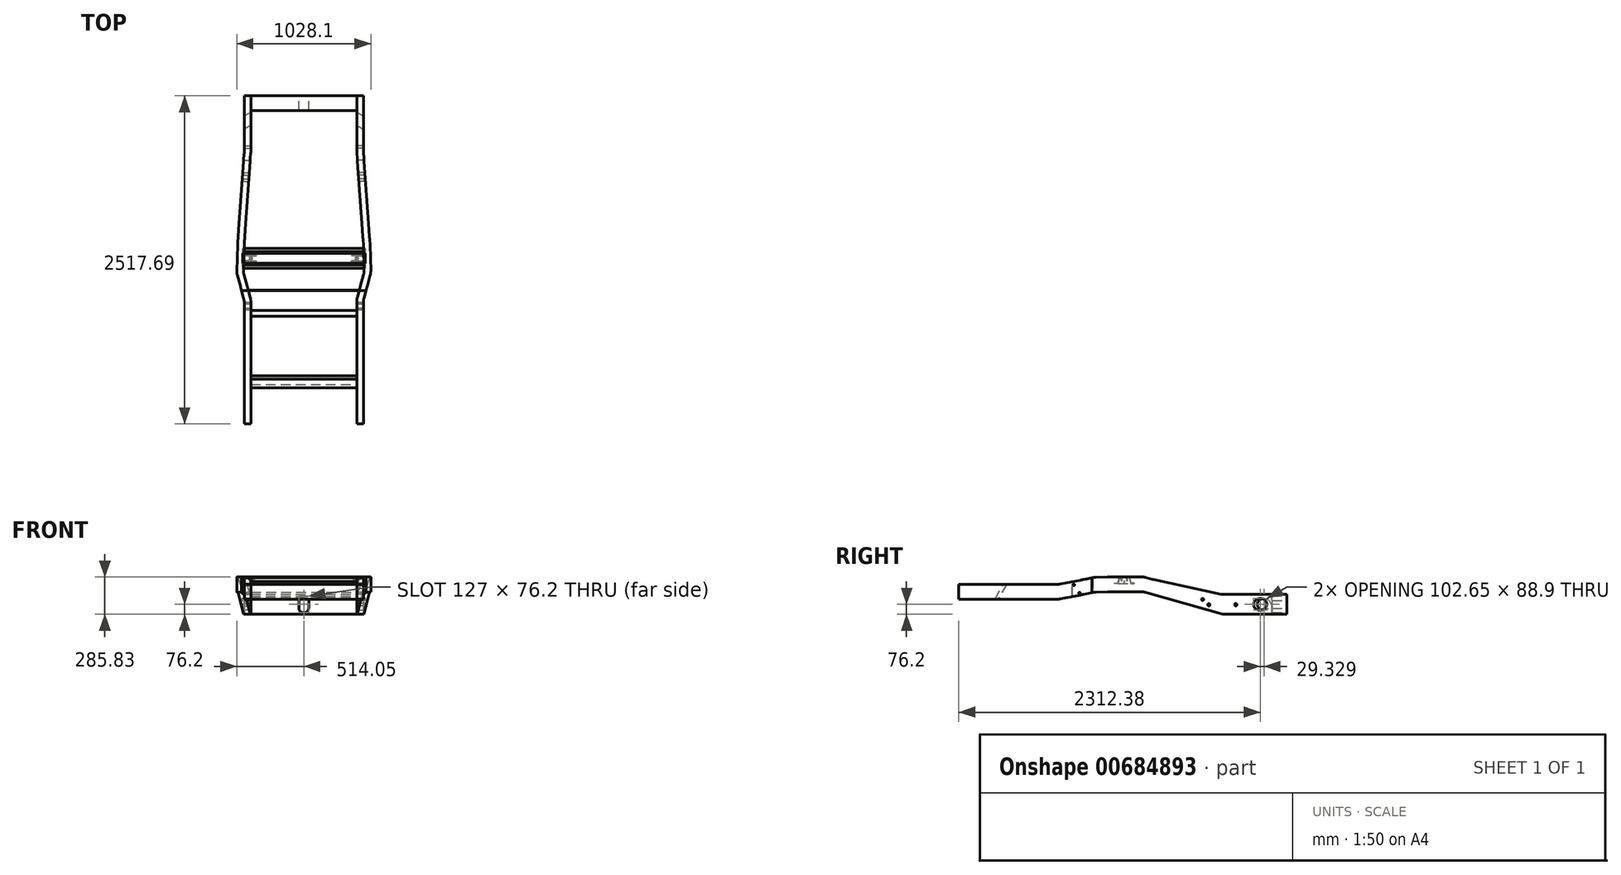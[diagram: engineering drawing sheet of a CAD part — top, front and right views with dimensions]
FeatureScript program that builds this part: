
annotation { "Feature Type Name" : "Feature", "Feature Type Description" : "" }
export const myFeature = defineFeature(function(context is Context, id is Id, definition is map)
    precondition{}
    {
        {
            var Q0;
            Q0=qCreatedBy(makeId("Top.planeOp"),FACE);
            var sketch = newSketch(context, id + "F0", { "sketchPlane" : qUnion([Q0])});
            skLineSegment(sketch, "E0", {"start": v(0, 1936.1) * mm, "end": v(0, -5906.31) * mm, "construction": true});
            skLineSegment(sketch, "E1", {"start": v(431.8, 0) * mm, "end": v(431.8, -431.8) * mm});
            skLineSegment(sketch, "E2", {"start": v(431.8, -431.8) * mm, "end": v(482.6, -1141.18) * mm});
            skLineSegment(sketch, "E3", {"start": v(482.6, -1141.18) * mm, "end": v(488.95, -1356.99) * mm});
            skLineSegment(sketch, "E4", {"start": v(488.95, -1356.99) * mm, "end": v(431.8, -1565.19) * mm});
            skLineSegment(sketch, "E5", {"start": v(431.8, -1565.19) * mm, "end": v(431.8, -2517.69) * mm});
            skLineSegment(sketch, "E6", {"start": v(431.8, -431.8) * mm, "end": v(431.8, -1285.92) * mm, "construction": true});
            skSolve(sketch);
        }
        {
            var Q0;
            Q0=qCreatedBy(makeId("Front.planeOp"),FACE);
            var Q1;
            Q1=sQuery(id+"F0.wireOp",VERTEX,"E1.start");
            cPlane(context, id + "F1", {"entities" : qUnion([Q0, Q1]), "cplaneType" : CPlaneType.PLANE_POINT, "offset" : 25.4 * mm, "width" : 152.4 * mm, "height" : 152.4 * mm});
        }
        {
            var Q0;
            Q0=qCreatedBy(id+"F1.planeOp",FACE);
            var sketch = newSketch(context, id + "F2", { "sketchPlane" : qUnion([Q0])});
            skLineSegment(sketch, "E7.bottom", {"start": v(406.4, 203.2) * mm, "end": v(457.2, 203.2) * mm});
            skLineSegment(sketch, "E7.top", {"start": v(406.4, -203.2) * mm, "end": v(457.2, -203.2) * mm});
            skLineSegment(sketch, "E7.left", {"start": v(406.4, 203.2) * mm, "end": v(406.4, -203.2) * mm});
            skLineSegment(sketch, "E7.right", {"start": v(457.2, 203.2) * mm, "end": v(457.2, -203.2) * mm});
            skPoint(sketch, "E7.middle", {"position": v(431.8, 0) * mm});
            skLineSegment(sketch, "E8", {"start": v(0, 0) * mm, "end": v(572.75, 0) * mm, "construction": true});
            skSolve(sketch);
        }
        {
            var Q0;
            Q0 = qSketchRegion(id + "F2", true);
            var Q1;
            Q1 = qConstructionFilter(qBodyType(qCreatedBy(id + "F0" ,EDGE), BodyType.WIRE), ConstructionObject.NO);
            sweep(context, id + "F3", {"profiles" : qUnion([Q0]), "path" : qUnion([Q1])});
        }
        {
            var Q0;
            Q0=qCreatedBy(makeId("Right.planeOp"),FACE);
            var sketch = newSketch(context, id + "F4", { "sketchPlane" : qUnion([Q0])});
            skLineSegment(sketch, "E9", {"start": v(0, -203.2) * mm, "end": v(-493.71, -203.2) * mm});
            skLineSegment(sketch, "E10", {"start": v(-493.71, -203.2) * mm, "end": v(-1091.9, -31.67) * mm});
            skLineSegment(sketch, "E11", {"start": v(-1091.9, -31.67) * mm, "end": v(-1371.3, -31.67) * mm});
            skLineSegment(sketch, "E12", {"start": v(-1371.3, -31.67) * mm, "end": v(-1472.9, -33.44) * mm});
            skLineSegment(sketch, "E13", {"start": v(-1371.3, -31.67) * mm, "end": v(-1529.34, -31.67) * mm, "construction": true});
            skLineSegment(sketch, "E14", {"start": v(-1472.9, -33.44) * mm, "end": v(-1747.16, -86.76) * mm});
            skLineSegment(sketch, "E15", {"start": v(-1747.16, -86.76) * mm, "end": v(-2517.69, -86.76) * mm});
            skLineSegment(sketch, "E16", {"start": v(-2517.69, -86.76) * mm, "end": v(-2517.69, -253.61) * mm});
            skLineSegment(sketch, "E17", {"start": v(-2517.69, -253.61) * mm, "end": v(0, -269.23) * mm});
            skLineSegment(sketch, "E18", {"start": v(0, -269.23) * mm, "end": v(0, -203.2) * mm});
            skLineSegment(sketch, "E19", {"start": v(0, -50.8) * mm, "end": v(-493.71, -50.8) * mm});
            skLineSegment(sketch, "E20", {"start": v(-493.71, -50.8) * mm, "end": v(-1028.7, 64.5) * mm});
            skLineSegment(sketch, "E21", {"start": v(-1028.7, 64.5) * mm, "end": v(-1028.7, -49.8) * mm, "construction": true});
            skLineSegment(sketch, "E22", {"start": v(-1091.9, -31.67) * mm, "end": v(-1091.9, 82.63) * mm, "construction": true});
            skLineSegment(sketch, "E23", {"start": v(-1371.3, -31.67) * mm, "end": v(-1371.3, 82.63) * mm, "construction": true});
            skLineSegment(sketch, "E24", {"start": v(-1472.9, -33.44) * mm, "end": v(-1472.9, 80.86) * mm, "construction": true});
            skLineSegment(sketch, "E25", {"start": v(-1747.16, -86.76) * mm, "end": v(-1747.16, 27.54) * mm, "construction": true});
            skLineSegment(sketch, "E26", {"start": v(-1028.7, 64.5) * mm, "end": v(-1091.9, 82.63) * mm});
            skLineSegment(sketch, "E27", {"start": v(-1091.9, 82.63) * mm, "end": v(-1371.3, 82.63) * mm});
            skLineSegment(sketch, "E28", {"start": v(-1472.9, 80.86) * mm, "end": v(-1747.16, 27.54) * mm});
            skLineSegment(sketch, "E29", {"start": v(-1472.9, 80.86) * mm, "end": v(-1371.3, 82.63) * mm});
            skLineSegment(sketch, "E30", {"start": v(-2517.69, -86.76) * mm, "end": v(-2517.69, 27.54) * mm, "construction": true});
            skLineSegment(sketch, "E31", {"start": v(-1747.16, 27.54) * mm, "end": v(-2517.69, 27.54) * mm});
            skLineSegment(sketch, "E32", {"start": v(-2517.69, 27.54) * mm, "end": v(-2517.69, 524.74) * mm});
            skLineSegment(sketch, "E33", {"start": v(-2517.69, 524.74) * mm, "end": v(0, 524.74) * mm});
            skLineSegment(sketch, "E34", {"start": v(0, 524.74) * mm, "end": v(0, -50.8) * mm});
            skSolve(sketch);
        }
        {
            var Q0;
            Q0 = qSketchRegion(id + "F4", true);
            var Q1;
            Q1=makeQuery(id+"F3.opSweep","SWEPT_FACE",FACE,{"disambiguationData":[OSD([sQuery(id+"F0.wireOp",EDGE,"1umSsKEu-dJId-BIwL-yde3-wRK5SwyTBX2N"),sQuery(id+"F2.wireOp",EDGE,"E7.right")])]});
            extrude(context, id + "F5", {"entities" : qUnion([Q0]), "operationType" : NewBodyOperationType.REMOVE, "depth" : 609.6 * mm, "endBoundEntityFace" : qUnion([Q1]), "offsetDistance" : 25.4 * mm});
        }
        {
            var Q0;
            Q0=makeQuery(id+"F3.opSweep","SWEPT_FACE",FACE,{"disambiguationData":[OSD([sQuery(id+"F0.wireOp",EDGE,"E1"),sQuery(id+"F2.wireOp",EDGE,"E7.left")])]});
            var sketch = newSketch(context, id + "F6", { "sketchPlane" : qUnion([Q0])});
            skLineSegment(sketch, "E35", {"start": v(-416.37, -129.41) * mm, "end": v(600.08, -129.41) * mm, "construction": true});
            skLineSegment(sketch, "E36", {"start": v(393.7, 39.46) * mm, "end": v(393.7, -270.74) * mm, "construction": true});
            skLineSegment(sketch, "E37", {"start": v(393.7, -88.9) * mm, "end": v(863.06, -88.9) * mm, "construction": true});
            skLineSegment(sketch, "E38", {"start": v(600.08, 71) * mm, "end": v(600.08, -269.25) * mm, "construction": true});
            skLineSegment(sketch, "E39", {"start": v(647.7, 77.42) * mm, "end": v(647.7, -282.1) * mm, "construction": true});
            skCircle(sketch, "E40", {"center": v(600.08, -129.41) * mm, "radius": 8.9 * mm});
            skCircle(sketch, "E41", {"center": v(647.7, -88.9) * mm, "radius": 8.9 * mm});
            skCircle(sketch, "E42", {"center": v(393.7, -129.41) * mm, "radius": 8.9 * mm});
            skSolve(sketch);
        }
        {
            var Q0;
            Q0 = qSketchRegion(id + "F6", true);
            extrude(context, id + "F7", {"entities" : qUnion([Q0]), "operationType" : NewBodyOperationType.REMOVE, "oppositeDirection" : true, "depth" : 508 * mm, "offsetDistance" : 25.4 * mm, "symmetric" : true});
        }
        {
            var Q0;
            Q0=makeQuery(id+"F5.boolean.opBoolean","COPY",EDGE,{"derivedFrom":makeQuery(id+"F5.opExtrude","SWEPT_EDGE",EDGE,{"disambiguationData":[OSD([sQuery(id+"F4.wireOp",EDGE,"E19"),sQuery(id+"F4.wireOp",EDGE,"E20")])]})});
            var Q1;
            Q1=makeQuery(id+"F3.opSweep","MID_CAP_EDGE",EDGE,{"disambiguationData":[OSD([sQuery(id+"F0.wireOp",VERTEX,"E2.start"),sQuery(id+"F2.wireOp",EDGE,"E7.left")])],"capPos":1.0});
            var Q2;
            Q2=makeQuery(id+"F5.boolean.opBoolean","COPY",EDGE,{"derivedFrom":makeQuery(id+"F5.opExtrude","SWEPT_EDGE",EDGE,{"disambiguationData":[OSD([sQuery(id+"F4.wireOp",EDGE,"E20"),sQuery(id+"F4.wireOp",EDGE,"E26")])]})});
            var Q3;
            Q3=makeQuery(id+"F5.boolean.opBoolean","COPY",EDGE,{"derivedFrom":makeQuery(id+"F5.opExtrude","SWEPT_EDGE",EDGE,{"disambiguationData":[OSD([sQuery(id+"F4.wireOp",EDGE,"E26"),sQuery(id+"F4.wireOp",EDGE,"E27")])]})});
            var Q4;
            Q4=makeQuery(id+"F3.opSweep","MID_CAP_EDGE",EDGE,{"disambiguationData":[OSD([sQuery(id+"F0.wireOp",VERTEX,"E3.start"),sQuery(id+"F2.wireOp",EDGE,"E7.left")])],"capPos":2.0});
            var Q5;
            Q5=makeQuery(id+"F5.boolean.opBoolean","COPY",EDGE,{"derivedFrom":makeQuery(id+"F5.opExtrude","SWEPT_EDGE",EDGE,{"disambiguationData":[OSD([sQuery(id+"F4.wireOp",EDGE,"E27"),sQuery(id+"F4.wireOp",EDGE,"E29")])]})});
            var Q6;
            Q6=makeQuery(id+"F5.boolean.opBoolean","COPY",EDGE,{"derivedFrom":makeQuery(id+"F5.opExtrude","SWEPT_EDGE",EDGE,{"disambiguationData":[OSD([sQuery(id+"F4.wireOp",EDGE,"E28"),sQuery(id+"F4.wireOp",EDGE,"E29")])]})});
            var Q7;
            Q7=makeQuery(id+"F3.opSweep","MID_CAP_EDGE",EDGE,{"disambiguationData":[OSD([sQuery(id+"F0.wireOp",VERTEX,"E4.start"),sQuery(id+"F2.wireOp",EDGE,"E7.left")])],"capPos":3.0});
            var Q8;
            Q8=makeQuery(id+"F3.opSweep","MID_CAP_EDGE",EDGE,{"disambiguationData":[OSD([sQuery(id+"F0.wireOp",VERTEX,"E5.start"),sQuery(id+"F2.wireOp",EDGE,"E7.left")])],"capPos":4.0});
            var Q9;
            Q9=makeQuery(id+"F5.boolean.opBoolean","COPY",EDGE,{"derivedFrom":makeQuery(id+"F5.opExtrude","SWEPT_EDGE",EDGE,{"disambiguationData":[OSD([sQuery(id+"F4.wireOp",EDGE,"E28"),sQuery(id+"F4.wireOp",EDGE,"E31")])]})});
            var Q10;
            Q10=makeQuery(id+"F5.boolean.opBoolean","COPY",EDGE,{"derivedFrom":makeQuery(id+"F5.opExtrude","SWEPT_EDGE",EDGE,{"disambiguationData":[OSD([sQuery(id+"F4.wireOp",EDGE,"E14"),sQuery(id+"F4.wireOp",EDGE,"E15")])]})});
            var Q11;
            Q11=makeQuery(id+"F5.boolean.opBoolean","COPY",EDGE,{"derivedFrom":makeQuery(id+"F5.opExtrude","SWEPT_EDGE",EDGE,{"disambiguationData":[OSD([sQuery(id+"F4.wireOp",EDGE,"E12"),sQuery(id+"F4.wireOp",EDGE,"E14")])]})});
            var Q12;
            Q12=makeQuery(id+"F5.boolean.opBoolean","COPY",EDGE,{"derivedFrom":makeQuery(id+"F5.opExtrude","SWEPT_EDGE",EDGE,{"disambiguationData":[OSD([sQuery(id+"F4.wireOp",EDGE,"E11"),sQuery(id+"F4.wireOp",EDGE,"E12")])]})});
            var Q13;
            Q13=makeQuery(id+"F5.boolean.opBoolean","COPY",EDGE,{"derivedFrom":makeQuery(id+"F5.opExtrude","SWEPT_EDGE",EDGE,{"disambiguationData":[OSD([sQuery(id+"F4.wireOp",EDGE,"E10"),sQuery(id+"F4.wireOp",EDGE,"E11")])]})});
            var Q14;
            Q14=makeQuery(id+"F5.boolean.opBoolean","COPY",EDGE,{"derivedFrom":makeQuery(id+"F5.opExtrude","SWEPT_EDGE",EDGE,{"disambiguationData":[OSD([sQuery(id+"F4.wireOp",EDGE,"E9"),sQuery(id+"F4.wireOp",EDGE,"E10")])]})});
            var Q15;
            Q15=makeQuery(id+"F3.opSweep","MID_CAP_EDGE",EDGE,{"disambiguationData":[OSD([sQuery(id+"F0.wireOp",VERTEX,"E2.start"),sQuery(id+"F2.wireOp",EDGE,"E7.right")])],"capPos":1.0});
            var Q16;
            Q16=makeQuery(id+"F3.opSweep","MID_CAP_EDGE",EDGE,{"disambiguationData":[OSD([sQuery(id+"F0.wireOp",VERTEX,"E3.start"),sQuery(id+"F2.wireOp",EDGE,"E7.right")])],"capPos":2.0});
            var Q17;
            Q17=makeQuery(id+"F3.opSweep","MID_CAP_EDGE",EDGE,{"disambiguationData":[OSD([sQuery(id+"F0.wireOp",VERTEX,"E4.start"),sQuery(id+"F2.wireOp",EDGE,"E7.right")])],"capPos":3.0});
            var Q18;
            Q18=makeQuery(id+"F3.opSweep","MID_CAP_EDGE",EDGE,{"disambiguationData":[OSD([sQuery(id+"F0.wireOp",VERTEX,"E5.start"),sQuery(id+"F2.wireOp",EDGE,"E7.right")])],"capPos":4.0});
            fillet(context, id + "F8", {"entities" : qUnion([Q0, Q1, Q2, Q3, Q4, Q5, Q6, Q7, Q8, Q9, Q10, Q11, Q12, Q13, Q14, Q15, Q16, Q17, Q18]), "radius" : 101.6 * mm, "tangentPropagation" : true, "allowEdgeOverflow" : false});
        }
        {
            var Q0;
            Q0=makeQuery(id+"F3.opSweep","SWEPT_BODY",BODY,{"disambiguationData":[OSD([sQuery(id+"F0.wireOp",EDGE,"zRG0IsD7-SMmf-8p0A-3XBu-xbHUB45AKsED"),sQuery(id+"F2.wireOp",EDGE,"E7.bottom"),sQuery(id+"F2.wireOp",EDGE,"E7.top"),sQuery(id+"F2.wireOp",EDGE,"E7.left"),sQuery(id+"F2.wireOp",EDGE,"E7.right")])]});
            var Q1;
            Q1=qCreatedBy(makeId("Right.planeOp"),FACE);
            mirror(context, id + "F9", {"entities" : qUnion([Q0]), "mirrorPlane" : qUnion([Q1])});
        }
        {
            var Q0;
            Q0=qCreatedBy(makeId("Right.planeOp"),FACE);
            var sketch = newSketch(context, id + "F10", { "sketchPlane" : qUnion([Q0])});
            skLineSegment(sketch, "E43", {"start": v(-2517.69, -86.76) * mm, "end": v(-1635.04, -86.76) * mm, "construction": true});
            skLineSegment(sketch, "E44", {"start": v(-1635.04, -86.76) * mm, "end": v(-1635.04, 22.37) * mm, "construction": true});
            skCircle(sketch, "E45", {"center": v(-1635.04, 22.37) * mm, "radius": 6.67 * mm});
            skCircle(sketch, "E46", {"center": v(-1590.59, -41.13) * mm, "radius": 6.67 * mm});
            skSolve(sketch);
        }
        {
            var Q0;
            Q0 = qSketchRegion(id + "F10", true);
            extrude(context, id + "F11", {"entities" : qUnion([Q0]), "operationType" : NewBodyOperationType.REMOVE, "oppositeDirection" : true, "depth" : 1016 * mm, "offsetDistance" : 25.4 * mm, "symmetric" : true});
        }
        {
            var Q0;
            Q0=makeQuery(id+"F3.opSweep","SWEPT_FACE",FACE,{"disambiguationData":[OSD([sQuery(id+"F0.wireOp",EDGE,"E1"),sQuery(id+"F2.wireOp",EDGE,"E7.left")])]});
            var sketch = newSketch(context, id + "F12", { "sketchPlane" : qUnion([Q0])});
            skLineSegment(sketch, "E47.bottom", {"start": v(0, -50.8) * mm, "end": v(114.3, -50.8) * mm});
            skLineSegment(sketch, "E47.top", {"start": v(0, -203.2) * mm, "end": v(114.3, -203.2) * mm});
            skLineSegment(sketch, "E47.left", {"start": v(0, -50.8) * mm, "end": v(0, -203.2) * mm});
            skLineSegment(sketch, "E47.right", {"start": v(114.3, -50.8) * mm, "end": v(114.3, -203.2) * mm});
            skSolve(sketch);
        }
        {
            var Q0;
            Q0 = qSketchRegion(id + "F12", true);
            var Q1;
            Q1=makeQuery(id+"F9.opPattern","COPY",FACE,{"derivedFrom":makeQuery(id+"F3.opSweep","SWEPT_FACE",FACE,{"disambiguationData":[OSD([sQuery(id+"F0.wireOp",EDGE,"E1"),sQuery(id+"F2.wireOp",EDGE,"E7.left")])]}),"instanceName":"1"});
            extrude(context, id + "F13", {"entities" : qUnion([Q0]), "endBound" : BoundingType.UP_TO_SURFACE, "depth" : 25.4 * mm, "endBoundEntityFace" : qUnion([Q1]), "offsetDistance" : 25.4 * mm});
        }
        {
            var Q0;
            Q0=makeQuery(id+"F3.opSweep","SWEPT_FACE",FACE,{"disambiguationData":[OSD([sQuery(id+"F0.wireOp",EDGE,"E5"),sQuery(id+"F2.wireOp",EDGE,"E7.left")])]});
            var sketch = newSketch(context, id + "F14", { "sketchPlane" : qUnion([Q0])});
            skLineSegment(sketch, "E48", {"start": v(2174.79, 27.54) * mm, "end": v(2240.78, -86.76) * mm});
            skLineSegment(sketch, "E49", {"start": v(2240.78, -86.76) * mm, "end": v(2215.38, -86.76) * mm});
            skLineSegment(sketch, "E50", {"start": v(2215.38, -86.76) * mm, "end": v(2149.39, 27.54) * mm});
            skLineSegment(sketch, "E51", {"start": v(2149.39, 27.54) * mm, "end": v(2174.79, 27.54) * mm});
            skSolve(sketch);
        }
        {
            var Q0;
            Q0 = qSketchRegion(id + "F14", true);
            var Q1;
            Q1=makeQuery(id+"F9.opPattern","COPY",FACE,{"derivedFrom":makeQuery(id+"F3.opSweep","SWEPT_FACE",FACE,{"disambiguationData":[OSD([sQuery(id+"F0.wireOp",EDGE,"E5"),sQuery(id+"F2.wireOp",EDGE,"E7.left")])]}),"instanceName":"1"});
            extrude(context, id + "F15", {"entities" : qUnion([Q0]), "endBound" : BoundingType.UP_TO_SURFACE, "depth" : 25.4 * mm, "endBoundEntityFace" : qUnion([Q1]), "offsetDistance" : 25.4 * mm});
        }
        {
            var Q0;
            Q0=makeQuery(id+"F3.opSweep","SWEPT_FACE",FACE,{"disambiguationData":[OSD([sQuery(id+"F0.wireOp",EDGE,"E5"),sQuery(id+"F2.wireOp",EDGE,"E7.left")])]});
            var sketch = newSketch(context, id + "F16", { "sketchPlane" : qUnion([Q0])});
            skLineSegment(sketch, "E52", {"start": v(1692.19, 38.23) * mm, "end": v(1645.44, 47.32) * mm});
            skLineSegment(sketch, "E53", {"start": v(1645.44, 47.32) * mm, "end": v(1645.44, -66.98) * mm});
            skLineSegment(sketch, "E54", {"start": v(1645.44, -66.98) * mm, "end": v(1692.19, -76.07) * mm});
            skLineSegment(sketch, "E55", {"start": v(1692.19, -76.07) * mm, "end": v(1692.19, -72.97) * mm});
            skLineSegment(sketch, "E56", {"start": v(1648.49, 43.62) * mm, "end": v(1692.19, 35.12) * mm});
            skLineSegment(sketch, "E57", {"start": v(1692.19, 35.12) * mm, "end": v(1692.19, 38.23) * mm});
            skLineSegment(sketch, "E58", {"start": v(1692.19, -72.97) * mm, "end": v(1648.49, -64.47) * mm});
            skLineSegment(sketch, "E59", {"start": v(1648.49, 43.62) * mm, "end": v(1648.49, -64.47) * mm});
            skSolve(sketch);
        }
        {
            var Q0;
            Q0 = qSketchRegion(id + "F16", true);
            var Q1;
            Q1=makeQuery(id+"F9.opPattern","COPY",FACE,{"derivedFrom":makeQuery(id+"F3.opSweep","SWEPT_FACE",FACE,{"disambiguationData":[OSD([sQuery(id+"F0.wireOp",EDGE,"E5"),sQuery(id+"F2.wireOp",EDGE,"E7.left")])]}),"instanceName":"1"});
            extrude(context, id + "F17", {"entities" : qUnion([Q0]), "endBound" : BoundingType.UP_TO_SURFACE, "depth" : 25.4 * mm, "endBoundEntityFace" : qUnion([Q1]), "offsetDistance" : 25.4 * mm});
        }
        {
            var Q0;
            Q0=qCreatedBy(makeId("Right.planeOp"),FACE);
            var sketch = newSketch(context, id + "F18", { "sketchPlane" : qUnion([Q0])});
            skLineSegment(sketch, "E60", {"start": v(-1247.69, 150.62) * mm, "end": v(-1247.69, -76.38) * mm, "construction": true});
            skLineSegment(sketch, "E61", {"start": v(-1247.69, 82.63) * mm, "end": v(-1285.79, 82.63) * mm});
            skLineSegment(sketch, "E62", {"start": v(-1285.79, 82.63) * mm, "end": v(-1298.58, 34.88) * mm});
            skLineSegment(sketch, "E63", {"start": v(-1323.89, 34.88) * mm, "end": v(-1298.58, 34.88) * mm});
            skLineSegment(sketch, "E64", {"start": v(-1323.89, 34.88) * mm, "end": v(-1323.89, 31.83) * mm});
            skLineSegment(sketch, "E65", {"start": v(-1296.24, 31.83) * mm, "end": v(-1323.89, 31.83) * mm});
            skLineSegment(sketch, "E66", {"start": v(-1296.24, 31.83) * mm, "end": v(-1283.45, 79.58) * mm});
            skLineSegment(sketch, "E67", {"start": v(-1283.45, 79.58) * mm, "end": v(-1247.69, 79.58) * mm});
            skLineSegment(sketch, "E68.MirrorCS", {"start": v(-1171.49, 34.88) * mm, "end": v(-1171.49, 31.83) * mm});
            skLineSegment(sketch, "E69.MirrorCS", {"start": v(-1199.13, 31.83) * mm, "end": v(-1171.49, 31.83) * mm});
            skLineSegment(sketch, "E70.MirrorCS", {"start": v(-1171.49, 34.88) * mm, "end": v(-1196.8, 34.88) * mm});
            skLineSegment(sketch, "E71.MirrorCS", {"start": v(-1209.59, 82.63) * mm, "end": v(-1196.8, 34.88) * mm});
            skLineSegment(sketch, "E72.MirrorCS", {"start": v(-1199.13, 31.83) * mm, "end": v(-1211.93, 79.58) * mm});
            skLineSegment(sketch, "E73.MirrorCS", {"start": v(-1247.69, 82.63) * mm, "end": v(-1209.59, 82.63) * mm});
            skLineSegment(sketch, "E74.MirrorCS", {"start": v(-1211.93, 79.58) * mm, "end": v(-1247.69, 79.58) * mm});
            skSolve(sketch);
        }
        {
            var Q0;
            Q0 = qSketchRegion(id + "F18", true);
            extrude(context, id + "F19", {"entities" : qUnion([Q0]), "depth" : 939.8 * mm, "offsetDistance" : 25.4 * mm, "symmetric" : true});
        }
        {
            var Q0;
            Q0=makeQuery(id+"F13.opExtrude","SWEPT_FACE",FACE,{"disambiguationData":[OSD([sQuery(id+"F12.wireOp",EDGE,"E47.left")])]});
            var sketch = newSketch(context, id + "F20", { "sketchPlane" : qUnion([Q0])});
            skLineSegment(sketch, "E75", {"start": v(0, -50.8) * mm, "end": v(0, -203.2) * mm, "construction": true});
            skLineSegment(sketch, "E76", {"start": v(-55.42, -127) * mm, "end": v(70.2, -127) * mm, "construction": true});
            skPoint(sketch, "E76.startSnap0", {"position": v(0, -127) * mm});
            skArc(sketch, "E77", {"start": v(38.1, -97.33) * mm, "mid": v(0, -63.5) * mm, "end": v(-38.1, -97.33) * mm});
            skArc(sketch, "E78.MirrorC", {"start": v(38.1, -156.67) * mm, "mid": v(0, -190.5) * mm, "end": v(-38.1, -156.67) * mm});
            skLineSegment(sketch, "E79", {"start": v(-38.1, -97.33) * mm, "end": v(-38.1, -156.67) * mm});
            skLineSegment(sketch, "E80.MirrorCS", {"start": v(38.1, -97.33) * mm, "end": v(38.1, -156.67) * mm});
            skSolve(sketch);
        }
        {
            var Q0;
            Q0 = qSketchRegion(id + "F20", true);
            var Q1;
            Q1=makeQuery(id+"F13.opExtrude","SWEPT_FACE",FACE,{"disambiguationData":[OSD([sQuery(id+"F12.wireOp",EDGE,"E47.right")])]});
            extrude(context, id + "F21", {"entities" : qUnion([Q0]), "operationType" : NewBodyOperationType.REMOVE, "endBound" : BoundingType.UP_TO_SURFACE, "oppositeDirection" : true, "depth" : 25.4 * mm, "endBoundEntityFace" : qUnion([Q1]), "offsetDistance" : 25.4 * mm});
        }
        {
            var Q0;
            Q0=makeQuery(id+"F9.opPattern","COPY",FACE,{"derivedFrom":makeQuery(id+"F3.opSweep","CAP_FACE",FACE,{"disambiguationData":[OSD([sQuery(id+"F0.wireOp",VERTEX,"E5.end"),sQuery(id+"F2.wireOp",EDGE,"E7.bottom"),sQuery(id+"F2.wireOp",EDGE,"E7.top"),sQuery(id+"F2.wireOp",EDGE,"E7.left"),sQuery(id+"F2.wireOp",EDGE,"E7.right")])],"isStart":false}),"instanceName":"1"});
            cPlane(context, id + "F22", {"entities" : qUnion([Q0]), "cplaneType" : CPlaneType.OFFSET, "offset" : 1022.35 * mm, "oppositeDirection" : true, "width" : 152.4 * mm, "height" : 152.4 * mm});
        }
        {
            var Q0;
            Q0=qCreatedBy(id+"F22.planeOp",FACE);
            var sketch = newSketch(context, id + "F23", { "sketchPlane" : qUnion([Q0])});
            skLineSegment(sketch, "E81", {"start": v(-477.31, 76.5) * mm, "end": v(477.31, 76.5) * mm});
            skLineSegment(sketch, "E82", {"start": v(477.31, 76.5) * mm, "end": v(477.31, -37.8) * mm});
            skLineSegment(sketch, "E83", {"start": v(477.31, -37.8) * mm, "end": v(-477.31, -37.8) * mm});
            skLineSegment(sketch, "E84", {"start": v(-477.31, -37.8) * mm, "end": v(-477.31, 76.5) * mm});
            skSolve(sketch);
        }
        {
            var Q0;
            Q0 = qSketchRegion(id + "F23", true);
            extrude(context, id + "F24", {"entities" : qUnion([Q0]), "oppositeDirection" : true, "depth" : 4.76 * mm, "offsetDistance" : 25.4 * mm});
        }
        {
            var Q0;
            Q0=makeQuery(id+"F19.opExtrude","SWEPT_EDGE",EDGE,{"disambiguationData":[OSD([sQuery(id+"F18.wireOp",EDGE,"E70.MirrorCS"),sQuery(id+"F18.wireOp",EDGE,"E71.MirrorCS")])]});
            var Q1;
            Q1=qCreatedBy(makeId("Front.planeOp"),FACE);
            cPlane(context, id + "F25", {"entities" : qUnion([Q0, Q1]), "cplaneType" : CPlaneType.LINE_ANGLE, "offset" : 25.4 * mm, "angle" : 0 * degree, "width" : 152.4 * mm, "height" : 152.4 * mm});
        }
        {
            var Q0;
            Q0=makeQuery(id+"F19.opExtrude","SWEPT_FACE",FACE,{"disambiguationData":[OSD([sQuery(id+"F18.wireOp",EDGE,"E65")])]});
            var sketch = newSketch(context, id + "F26", { "sketchPlane" : qUnion([Q0])});
            skLineSegment(sketch, "E85", {"start": v(0, 1414.16) * mm, "end": v(0, 1082.26) * mm, "construction": true});
            skLineSegment(sketch, "E86", {"start": v(-415.93, 1296.24) * mm, "end": v(-415.93, 1199.13) * mm});
            skLineSegment(sketch, "E87", {"start": v(-406.4, 1323.76) * mm, "end": v(-406.4, 1158.82) * mm, "construction": true});
            skLineSegment(sketch, "E88", {"start": v(-411.16, 1296.24) * mm, "end": v(-411.16, 1199.13) * mm});
            skLineSegment(sketch, "E89", {"start": v(-415.93, 1296.24) * mm, "end": v(-411.16, 1296.24) * mm});
            skLineSegment(sketch, "E90", {"start": v(-411.16, 1199.13) * mm, "end": v(-415.93, 1199.13) * mm});
            skLineSegment(sketch, "E91.MirrorCS", {"start": v(-401.64, 1199.13) * mm, "end": v(-396.87, 1199.13) * mm});
            skLineSegment(sketch, "E92.MirrorCS", {"start": v(-396.87, 1296.24) * mm, "end": v(-396.87, 1199.13) * mm});
            skLineSegment(sketch, "E93.MirrorCS", {"start": v(-401.64, 1296.24) * mm, "end": v(-401.64, 1199.13) * mm});
            skLineSegment(sketch, "E94.MirrorCS", {"start": v(-396.87, 1296.24) * mm, "end": v(-401.64, 1296.24) * mm});
            skLineSegment(sketch, "E95.MirrorCS", {"start": v(411.16, 1199.13) * mm, "end": v(415.93, 1199.13) * mm});
            skLineSegment(sketch, "E96.MirrorCS", {"start": v(415.93, 1296.24) * mm, "end": v(411.16, 1296.24) * mm});
            skLineSegment(sketch, "E97.MirrorCS", {"start": v(401.64, 1199.13) * mm, "end": v(396.87, 1199.13) * mm});
            skLineSegment(sketch, "E98.MirrorCS", {"start": v(396.87, 1296.24) * mm, "end": v(401.64, 1296.24) * mm});
            skLineSegment(sketch, "E99.MirrorCS", {"start": v(396.87, 1296.24) * mm, "end": v(396.87, 1199.13) * mm});
            skLineSegment(sketch, "E100.MirrorCS", {"start": v(401.64, 1296.24) * mm, "end": v(401.64, 1199.13) * mm});
            skLineSegment(sketch, "E101.MirrorCS", {"start": v(415.93, 1296.24) * mm, "end": v(415.93, 1199.13) * mm});
            skLineSegment(sketch, "E102.MirrorCS", {"start": v(411.16, 1296.24) * mm, "end": v(411.16, 1199.13) * mm});
            skSolve(sketch);
        }
        {
            var Q0;
            Q0 = qSketchRegion(id + "F26", true);
            var Q1;
            Q1=makeQuery(id+"F19.opExtrude","SWEPT_FACE",FACE,{"disambiguationData":[OSD([sQuery(id+"F18.wireOp",EDGE,"E67"),sQuery(id+"F18.wireOp",EDGE,"E74.MirrorCS")])]});
            extrude(context, id + "F27", {"entities" : qUnion([Q0]), "operationType" : NewBodyOperationType.ADD, "endBound" : BoundingType.UP_TO_SURFACE, "oppositeDirection" : true, "depth" : 25.4 * mm, "endBoundEntityFace" : qUnion([Q1]), "offsetDistance" : 25.4 * mm});
        }
        {
            var Q0;
            {var subQ0=sQuery(id+"F26.wireOp",EDGE,"E86");Q0=makeQuery(id+"F27.boolean.opBoolean","SPLIT",FACE,{"disambiguationData":[TD([makeQuery(id+"F19.opExtrude","SWEPT_FACE",FACE,{"disambiguationData":[OSD([sQuery(id+"F18.wireOp",EDGE,"E65")])]})])],"derivedFrom":makeQuery(id+"F27.opExtrude","SWEPT_FACE",FACE,{"disambiguationData":[OSD([subQ0])]})});}
            var sketch = newSketch(context, id + "F28", { "sketchPlane" : qUnion([Q0])});
            skLineSegment(sketch, "E103", {"start": v(1247.69, 79.58) * mm, "end": v(1247.69, 31.83) * mm, "construction": true});
            skCircle(sketch, "E104", {"center": v(1247.69, 44.53) * mm, "radius": 3.81 * mm});
            skSolve(sketch);
        }
        {
            var Q0;
            Q0 = qSketchRegion(id + "F28", true);
            var Q1;
            {var subQ0=sQuery(id+"F26.wireOp",EDGE,"E101.MirrorCS");Q1=makeQuery(id+"F27.boolean.opBoolean","SPLIT",FACE,{"disambiguationData":[TD([makeQuery(id+"F19.opExtrude","SWEPT_FACE",FACE,{"disambiguationData":[OSD([sQuery(id+"F18.wireOp",EDGE,"E65")])]})])],"derivedFrom":makeQuery(id+"F27.opExtrude","SWEPT_FACE",FACE,{"disambiguationData":[OSD([subQ0])]})});}
            extrude(context, id + "F29", {"entities" : qUnion([Q0]), "operationType" : NewBodyOperationType.REMOVE, "endBound" : BoundingType.UP_TO_SURFACE, "oppositeDirection" : true, "depth" : 25.4 * mm, "endBoundEntityFace" : qUnion([Q1]), "offsetDistance" : 25.4 * mm});
        }
        {
            var Q0;
            Q0=makeQuery(id+"F27.boolean.opBoolean","SPLIT",FACE,{"disambiguationData":[TD([makeQuery(id+"F19.opExtrude","SWEPT_FACE",FACE,{"disambiguationData":[OSD([sQuery(id+"F18.wireOp",EDGE,"E71.MirrorCS")])]})])],"derivedFrom":makeQuery(id+"F27.opExtrude","SWEPT_FACE",FACE,{"disambiguationData":[OSD([sQuery(id+"F26.wireOp",EDGE,"E86")])]})});
            var sketch = newSketch(context, id + "F30", { "sketchPlane" : qUnion([Q0])});
            skLineSegment(sketch, "E105", {"start": v(1199.13, 79.58) * mm, "end": v(1199.13, 43.6) * mm});
            skLineSegment(sketch, "E106", {"start": v(1199.13, 43.6) * mm, "end": v(1208.77, 79.58) * mm});
            skLineSegment(sketch, "E107", {"start": v(1208.77, 79.58) * mm, "end": v(1199.13, 79.58) * mm});
            skLineSegment(sketch, "E108", {"start": v(1247.69, 102.73) * mm, "end": v(1247.69, 16.87) * mm, "construction": true});
            skLineSegment(sketch, "E109.MirrorCS", {"start": v(1286.6, 79.58) * mm, "end": v(1296.24, 79.58) * mm});
            skLineSegment(sketch, "E110.MirrorCS", {"start": v(1296.24, 43.6) * mm, "end": v(1286.6, 79.58) * mm});
            skLineSegment(sketch, "E111.MirrorCS", {"start": v(1296.24, 79.58) * mm, "end": v(1296.24, 43.6) * mm});
            skSolve(sketch);
        }
        {
            var Q0;
            Q0 = qSketchRegion(id + "F30", true);
            var Q1;
            Q1=makeQuery(id+"F27.boolean.opBoolean","SPLIT",FACE,{"disambiguationData":[TD([makeQuery(id+"F19.opExtrude","SWEPT_FACE",FACE,{"disambiguationData":[OSD([sQuery(id+"F18.wireOp",EDGE,"E71.MirrorCS")])]})])],"derivedFrom":makeQuery(id+"F27.opExtrude","SWEPT_FACE",FACE,{"disambiguationData":[OSD([sQuery(id+"F26.wireOp",EDGE,"E101.MirrorCS")])]})});
            extrude(context, id + "F31", {"entities" : qUnion([Q0]), "operationType" : NewBodyOperationType.REMOVE, "endBound" : BoundingType.UP_TO_SURFACE, "oppositeDirection" : true, "depth" : 25.4 * mm, "endBoundEntityFace" : qUnion([Q1]), "offsetDistance" : 25.4 * mm});
        }
        {
            var Q0;
            Q0=makeQuery(id+"F27.boolean.opBoolean","SPLIT",FACE,{"disambiguationData":[TD([makeQuery(id+"F27.opExtrude","SWEPT_FACE",FACE,{"disambiguationData":[OSD([sQuery(id+"F26.wireOp",EDGE,"E92.MirrorCS")])]})])],"derivedFrom":makeQuery(id+"F19.opExtrude","SWEPT_FACE",FACE,{"disambiguationData":[OSD([sQuery(id+"F18.wireOp",EDGE,"E67"),sQuery(id+"F18.wireOp",EDGE,"E74.MirrorCS")])]})});
            var sketch = newSketch(context, id + "F32", { "sketchPlane" : qUnion([Q0])});
            skLineSegment(sketch, "E112", {"start": v(0, 1398.59) * mm, "end": v(0, 1073.54) * mm, "construction": true});
            skLineSegment(sketch, "E113", {"start": v(-406.4, 1296.24) * mm, "end": v(-406.4, 1199.13) * mm, "construction": true});
            skLineSegment(sketch, "E114.bottom", {"start": v(-396.87, 1270.75) * mm, "end": v(-365.12, 1270.75) * mm});
            skLineSegment(sketch, "E114.top", {"start": v(-396.87, 1265.99) * mm, "end": v(-365.12, 1265.99) * mm});
            skLineSegment(sketch, "E114.left", {"start": v(-396.87, 1270.75) * mm, "end": v(-396.87, 1265.99) * mm});
            skLineSegment(sketch, "E114.right", {"start": v(-365.12, 1270.75) * mm, "end": v(-365.12, 1265.99) * mm});
            skLineSegment(sketch, "E115", {"start": v(-436.97, 1247.69) * mm, "end": v(-376.03, 1247.69) * mm, "construction": true});
            skPoint(sketch, "E115.startSnap0", {"position": v(-406.4, 1247.69) * mm});
            skLineSegment(sketch, "E116.MirrorCS", {"start": v(-396.87, 1224.63) * mm, "end": v(-396.87, 1229.39) * mm});
            skLineSegment(sketch, "E117.MirrorCS", {"start": v(-396.87, 1224.63) * mm, "end": v(-365.12, 1224.63) * mm});
            skLineSegment(sketch, "E118.MirrorCS", {"start": v(-365.12, 1224.63) * mm, "end": v(-365.12, 1229.39) * mm});
            skLineSegment(sketch, "E119.MirrorCS", {"start": v(-396.87, 1229.39) * mm, "end": v(-365.12, 1229.39) * mm});
            skLineSegment(sketch, "E120.MirrorCS", {"start": v(-447.68, 1270.75) * mm, "end": v(-447.68, 1265.99) * mm});
            skLineSegment(sketch, "E121.MirrorCS", {"start": v(-415.93, 1224.63) * mm, "end": v(-415.93, 1229.39) * mm});
            skLineSegment(sketch, "E122.MirrorCS", {"start": v(-415.93, 1270.75) * mm, "end": v(-415.93, 1265.99) * mm});
            skLineSegment(sketch, "E123.MirrorCS", {"start": v(-447.68, 1224.63) * mm, "end": v(-447.68, 1229.39) * mm});
            skLineSegment(sketch, "E124.MirrorCS", {"start": v(-415.93, 1265.99) * mm, "end": v(-447.68, 1265.99) * mm});
            skLineSegment(sketch, "E125.MirrorCS", {"start": v(-415.93, 1224.63) * mm, "end": v(-447.68, 1224.63) * mm});
            skLineSegment(sketch, "E126.MirrorCS", {"start": v(-415.93, 1270.75) * mm, "end": v(-447.68, 1270.75) * mm});
            skLineSegment(sketch, "E127.MirrorCS", {"start": v(-415.93, 1229.39) * mm, "end": v(-447.68, 1229.39) * mm});
            skLineSegment(sketch, "E128.MirrorCS", {"start": v(415.93, 1224.63) * mm, "end": v(415.93, 1229.39) * mm});
            skLineSegment(sketch, "E129.MirrorCS", {"start": v(447.68, 1224.63) * mm, "end": v(447.68, 1229.39) * mm});
            skLineSegment(sketch, "E130.MirrorCS", {"start": v(447.68, 1270.75) * mm, "end": v(447.68, 1265.99) * mm});
            skLineSegment(sketch, "E131.MirrorCS", {"start": v(396.87, 1270.75) * mm, "end": v(396.87, 1265.99) * mm});
            skLineSegment(sketch, "E132.MirrorCS", {"start": v(415.93, 1270.75) * mm, "end": v(415.93, 1265.99) * mm});
            skLineSegment(sketch, "E133.MirrorCS", {"start": v(396.87, 1224.63) * mm, "end": v(396.87, 1229.39) * mm});
            skLineSegment(sketch, "E134.MirrorCS", {"start": v(365.12, 1224.63) * mm, "end": v(365.12, 1229.39) * mm});
            skLineSegment(sketch, "E135.MirrorCS", {"start": v(365.12, 1270.75) * mm, "end": v(365.12, 1265.99) * mm});
            skLineSegment(sketch, "E136.MirrorCS", {"start": v(396.87, 1265.99) * mm, "end": v(365.12, 1265.99) * mm});
            skLineSegment(sketch, "E137.MirrorCS", {"start": v(436.97, 1247.69) * mm, "end": v(376.03, 1247.69) * mm, "construction": true});
            skLineSegment(sketch, "E138.MirrorCS", {"start": v(415.93, 1270.75) * mm, "end": v(447.68, 1270.75) * mm});
            skLineSegment(sketch, "E139.MirrorCS", {"start": v(415.93, 1229.39) * mm, "end": v(447.68, 1229.39) * mm});
            skLineSegment(sketch, "E140.MirrorCS", {"start": v(396.87, 1270.75) * mm, "end": v(365.12, 1270.75) * mm});
            skPoint(sketch, "E141.MirrorP", {"position": v(406.4, 1247.69) * mm});
            skLineSegment(sketch, "E142.MirrorCS", {"start": v(396.87, 1224.63) * mm, "end": v(365.12, 1224.63) * mm});
            skLineSegment(sketch, "E143.MirrorCS", {"start": v(396.87, 1229.39) * mm, "end": v(365.12, 1229.39) * mm});
            skLineSegment(sketch, "E144.MirrorCS", {"start": v(415.93, 1265.99) * mm, "end": v(447.68, 1265.99) * mm});
            skLineSegment(sketch, "E145.MirrorCS", {"start": v(415.93, 1224.63) * mm, "end": v(447.68, 1224.63) * mm});
            skSolve(sketch);
        }
        {
            var Q0;
            Q0 = qSketchRegion(id + "F32", true);
            extrude(context, id + "F33", {"entities" : qUnion([Q0]), "operationType" : NewBodyOperationType.ADD, "depth" : 25.4 * mm, "offsetDistance" : 25.4 * mm});
        }
        {
            var Q0;
            Q0=makeQuery(id+"F33.opExtrude","SWEPT_FACE",FACE,{"disambiguationData":[OSD([sQuery(id+"F32.wireOp",EDGE,"E125.MirrorCS")])]});
            var sketch = newSketch(context, id + "F34", { "sketchPlane" : qUnion([Q0])});
            skLineSegment(sketch, "E146", {"start": v(415.92, 54.18) * mm, "end": v(447.67, 79.58) * mm});
            skLineSegment(sketch, "E147", {"start": v(447.67, 79.58) * mm, "end": v(447.67, 54.18) * mm});
            skLineSegment(sketch, "E148", {"start": v(447.67, 54.18) * mm, "end": v(415.92, 54.18) * mm});
            skLineSegment(sketch, "E149", {"start": v(365.12, 54.18) * mm, "end": v(365.12, 79.58) * mm});
            skLineSegment(sketch, "E150", {"start": v(365.12, 79.58) * mm, "end": v(396.87, 54.18) * mm});
            skLineSegment(sketch, "E151", {"start": v(396.87, 54.18) * mm, "end": v(365.12, 54.18) * mm});
            skLineSegment(sketch, "E152", {"start": v(-365.12, 54.18) * mm, "end": v(-396.87, 54.18) * mm});
            skLineSegment(sketch, "E153", {"start": v(-365.12, 54.18) * mm, "end": v(-365.12, 79.58) * mm});
            skLineSegment(sketch, "E154", {"start": v(-365.12, 79.58) * mm, "end": v(-396.87, 54.18) * mm});
            skLineSegment(sketch, "E155", {"start": v(-447.68, 54.18) * mm, "end": v(-447.68, 79.58) * mm});
            skLineSegment(sketch, "E156", {"start": v(-447.68, 79.58) * mm, "end": v(-415.93, 54.18) * mm});
            skLineSegment(sketch, "E157", {"start": v(-415.93, 54.18) * mm, "end": v(-447.68, 54.18) * mm});
            skSolve(sketch);
        }
        {
            var Q0;
            Q0 = qSketchRegion(id + "F34", true);
            var Q1;
            Q1=makeQuery(id+"F33.opExtrude","SWEPT_FACE",FACE,{"disambiguationData":[OSD([sQuery(id+"F32.wireOp",EDGE,"E114.bottom")])]});
            extrude(context, id + "F35", {"entities" : qUnion([Q0]), "operationType" : NewBodyOperationType.REMOVE, "endBound" : BoundingType.UP_TO_SURFACE, "oppositeDirection" : true, "depth" : 25.4 * mm, "endBoundEntityFace" : qUnion([Q1]), "offsetDistance" : 25.4 * mm});
        }
        {
            var Q0;
            Q0=qCreatedBy(makeId("Top.planeOp"),FACE);
            var sketch = newSketch(context, id + "F36", { "sketchPlane" : qUnion([Q0])});
            skLineSegment(sketch, "E158", {"start": v(0, 0) * mm, "end": v(-707.95, -408.74) * mm, "construction": true});
            skLineSegment(sketch, "E159", {"start": v(0, 0) * mm, "end": v(741.45, -428.08) * mm, "construction": true});
            skLineSegment(sketch, "E160", {"start": v(-603.54, -348.45) * mm, "end": v(-669.12, -234.86) * mm, "construction": true});
            skLineSegment(sketch, "E161", {"start": v(578.22, -333.84) * mm, "end": v(656.88, -197.6) * mm, "construction": true});
            skSolve(sketch);
        }
        {
            var Q0;
            Q0=sQuery(id+"F36.wireOp",EDGE,"E160");
            var Q1;
            Q1=qCreatedBy(makeId("Front.planeOp"),FACE);
            cPlane(context, id + "F37", {"entities" : qUnion([Q0, Q1]), "cplaneType" : CPlaneType.LINE_ANGLE, "offset" : 25.4 * mm, "angle" : 0 * degree, "width" : 152.4 * mm, "height" : 152.4 * mm});
        }
        {
            var Q0;
            Q0=sQuery(id+"F36.wireOp",EDGE,"E161");
            var Q1;
            Q1=qCreatedBy(makeId("Front.planeOp"),FACE);
            cPlane(context, id + "F38", {"entities" : qUnion([Q0, Q1]), "cplaneType" : CPlaneType.LINE_ANGLE, "offset" : 25.4 * mm, "angle" : 0 * degree, "width" : 152.4 * mm, "height" : 152.4 * mm});
        }
        {
            var Q0;
            Q0=qCreatedBy(id+"F37.planeOp",FACE);
            var sketch = newSketch(context, id + "F39", { "sketchPlane" : qUnion([Q0])});
            skLineSegment(sketch, "E162", {"start": v(228.6, -127) * mm, "end": v(36.87, -127) * mm, "construction": true});
            skCircle(sketch, "E163", {"center": v(50.8, -127) * mm, "radius": 44.45 * mm});
            skSolve(sketch);
        }
        {
            var Q0;
            Q0 = qSketchRegion(id + "F39", true);
            var Q1;
            Q1=makeQuery(id+"F9.opPattern","COPY",FACE,{"derivedFrom":makeQuery(id+"F3.opSweep","SWEPT_FACE",FACE,{"disambiguationData":[OSD([sQuery(id+"F0.wireOp",EDGE,"E1"),sQuery(id+"F2.wireOp",EDGE,"E7.left")])]}),"instanceName":"1"});
            extrude(context, id + "F40", {"entities" : qUnion([Q0]), "operationType" : NewBodyOperationType.REMOVE, "endBound" : BoundingType.UP_TO_SURFACE, "depth" : 25.4 * mm, "endBoundEntityFace" : qUnion([Q1]), "offsetDistance" : 25.4 * mm});
        }
        {
            var Q0;
            Q0=qCreatedBy(id+"F38.planeOp",FACE);
            var sketch = newSketch(context, id + "F41", { "sketchPlane" : qUnion([Q0])});
            skLineSegment(sketch, "E164", {"start": v(38.79, -127) * mm, "end": v(-228.6, -127) * mm, "construction": true});
            skCircle(sketch, "E165", {"center": v(-50.8, -127) * mm, "radius": 44.45 * mm});
            skSolve(sketch);
        }
        {
            var Q0;
            Q0 = qSketchRegion(id + "F41", true);
            var Q1;
            Q1=makeQuery(id+"F3.opSweep","SWEPT_FACE",FACE,{"disambiguationData":[OSD([sQuery(id+"F0.wireOp",EDGE,"E1"),sQuery(id+"F2.wireOp",EDGE,"E7.left")])]});
            extrude(context, id + "F42", {"entities" : qUnion([Q0]), "operationType" : NewBodyOperationType.REMOVE, "endBound" : BoundingType.UP_TO_SURFACE, "depth" : 25.4 * mm, "endBoundEntityFace" : qUnion([Q1]), "offsetDistance" : 25.4 * mm});
        }
    });
